# Revit family: Storage-Freestanding-Teknion-BFCL_Cubic_Tower_with_Solid_Doors-R2019
name_source: partatom
category: Furniture
units: mm (PartAtom-declared; Revit-internal decimal feet)

## family parameters
Always vertical = Yes
Cut with Voids When Loaded = No
OmniClass Number = 23.40.20.00
OmniClass Title = General Furniture and Specialties
Room Calculation Point = No
Shared = Yes
Work Plane-Based = No

## types (5) — shared parameters
Assembly Code = E2020200
Manufacturer = Teknion
Manufacturer Fax = 416.661.4586
Part Number = BFCL
Product Documentation Link = http://www.teknion.com
Product Line = Expansion Casegoods
Product Page URL = http://www.teknion.com
Series = Expansion Casegoods
Sustainability Data = http://www.teknion.com
URL = www.teknion.com
Unit Weight URL = http://www.teknion.com
Warranty = http://www.teknion.com

## per-type parameters (varying)
| type | 2D Elevation Bottom Door | 2D Elevation Top and Bottom Second Door | Description | File Drawers | First Lock | Fourth Lock | Fully Enclosed | Individual Doors | Model | Second Lock | Second Shelf Visibility | Semi-Opened | Third Lock | Wardrobe |
| Fully Enclosed, Wardrobe Storage Style, 18"w | Yes | No | Freestanding Cubic Tower with Solid Doors, Fully Enclosed, Wardrobe Storage Style, 18" Width | No | No | Yes | Yes | No | BFCLFW__18___ | Yes | Yes | No | No | Yes |
| Semi-Opened, Individual Doors Storage Style, 18"w | Yes | Yes | Freestanding Cubic Tower with Solid Doors, Semi-Opened, Individual Doors, 18" Width | No | Yes | Yes | No | Yes | BFCLOD__18___ | No | No | Yes | Yes | No |
| Fully Enclosed, Individual Doors Storage Style, 18"w | Yes | Yes | Freestanding Cubic Tower with Solid Doors, Fully Enclosed, Individual Doors Storage Style, 18" Width | No | Yes | Yes | Yes | Yes | BFCLFD__18___ | Yes | Yes | No | Yes | No |
| Semi-Opened, File Drawers Storage Style, 18"w | No | Yes | Freestanding Cubic Tower with Solid Doors, Semi-Opened, File Drawers Storage Style, 18" Width | Yes | Yes | No | No | No | BFCLOF__18___ | No | No | Yes | Yes | No |
| Fully Enclosed, File Drawers Storage Style, 18"w | No | Yes | Freestanding Cubic Tower with Solid Doors, Fully Enclosed, File Drawers Storage Style, 18" Width | Yes | Yes | No | Yes | No | BFCLFF__18___ | Yes | Yes | No | Yes | No |

## geometry (parser evidence)
native form markers: Blend x4, Sweep x3
no freeform markers — native parametric forms only
